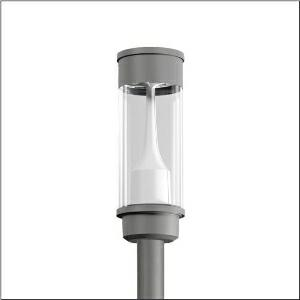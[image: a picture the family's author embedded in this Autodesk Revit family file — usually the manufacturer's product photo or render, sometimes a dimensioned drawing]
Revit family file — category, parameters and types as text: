
# Revit family: litepole_iq___p1_0a_5xa5415lf14h_d8b4
name_source: partatom
category: Lighting Fixtures
units: mm (PartAtom-declared; Revit-internal decimal feet)

## family parameters
Cut with Voids When Loaded = No
Host = Face
Light Source = No
Part Type = Normal
Room Calculation Point = No
Round Connector Dimension = Use Diameter
Shared = No

## types (1)
- --- (1 x LED, 1510 lm, 10 W, 4000K)
    Apparent Load = 10 VA
    CIE Flux Codes = 32 61 90 93 100
    Color Rendering = 70
    Color Temperature = 4000K
    Default Elevation = 1800 mm
    Description = Litepole iQ, mast luminaire, Module 540 iQ-SR, primary light control with 3 zone facetted reflector, of plastic, silver coated, highly specular, structured, primary optical cover: cover, of PMMA, transparent, partly coated, light distribution: P1.0a, light emission: direct distribution, primary light characteristic: strongly asymmetric, installation type: post-top, LED, High Power LED, rated luminous flux: 1.510lm, luminous efficacy: 151lm/W, light colour: 740, colour temperature: 4000K, control gear: iQ Street-Remote, control: optimised constant luminous flux control (CLO 2.0), Desk-Remote (wireless, voltage-free reading and setting of iQ features in the workshop via application-optimized NFC function/RFID function), Light-Fading, Smart-Wire, Night-Set, Lumen-Switch, Temp-Guard, Auto-Match, Street-Remote, pre-setting: logarithmic dimming characteristic, with terminal, 6-pole, max. 2.5mm², mains connection: 230..240V, AC, 50/60Hz, start of lifetime: 10W, end of service life: 10W, reduction: 5W, luminaire housing, upper part, of glass-fibre reinforced polyester, coated, Siteco® metallic grey (DB 702S), diameter: 210mm, height: 590mm, spigot size: d x l = 76 x 70mm (post-top) | with reducer (optional accessory) 60 x 70mm, mounting height: 3..5m, post-top mast mounting element, of diecast aluminium, coated, Siteco® metallic grey (DB 702S), Module 540 iQ-SR, traffic white (RAL 9016), equipment: standard, protection rating (complete): IP65, insulation class (complete): insulation class II (safety insulation), certification: CE, ENEC, VDE, packaging unit: 1 piece

Light Distribution: P1.0a
    Height = 590 mm
    Lamp = 1 x LED
    Lamp Light Flux = 1510 lm
    Lamp Power = 10 W
    Lamp count = 1
    Length = 220 mm
    Luminous efficacy = 151 lm/W
    Manufacturer = Siteco
    ModVariant = No
    Model = 5XA5415LF14H
    Number of Poles = 1
    OnlyDefault = Yes
    Power Factor = 1
    Product Name = Litepole iQ | P1.0a
    Product group = mast luminaire | pylon top
    ProductGroupID = 6100
    Protection Class = Protection class II
    Protection Degree = IP 65
    RLX_Detail_Level = 1
    RLX_Emergency_Light_Flux = 0 lm
    RLX_Emergency_Type = 0
    RLX_Emergency_Type_DB = No
    RlxData = <blob elided: 68405 chars, md5=9c93e489>
    Socket = socket
    Standby Power = 0 W
    System Light Flux = 1510 lm
    System Power = 10 W
    Type Comments = factory setting: luminous flux: 100 % | dim-lin: 254 | 401 mA
    Type Image = l_1006025.jpg
    URL = http://relux.com
    VarID = @adj_158175
    Voltage = 0 V
    Weight = 0.00 kg
    Width = 0 mm  [stored 0 ft]

note: [stored X ft] marks values corroborated as IEEE doubles in the binary element streams (Revit-internal decimal feet)

## geometry (parser evidence)
native form markers: Blend x4, Sweep x14
no freeform markers — native parametric forms only
